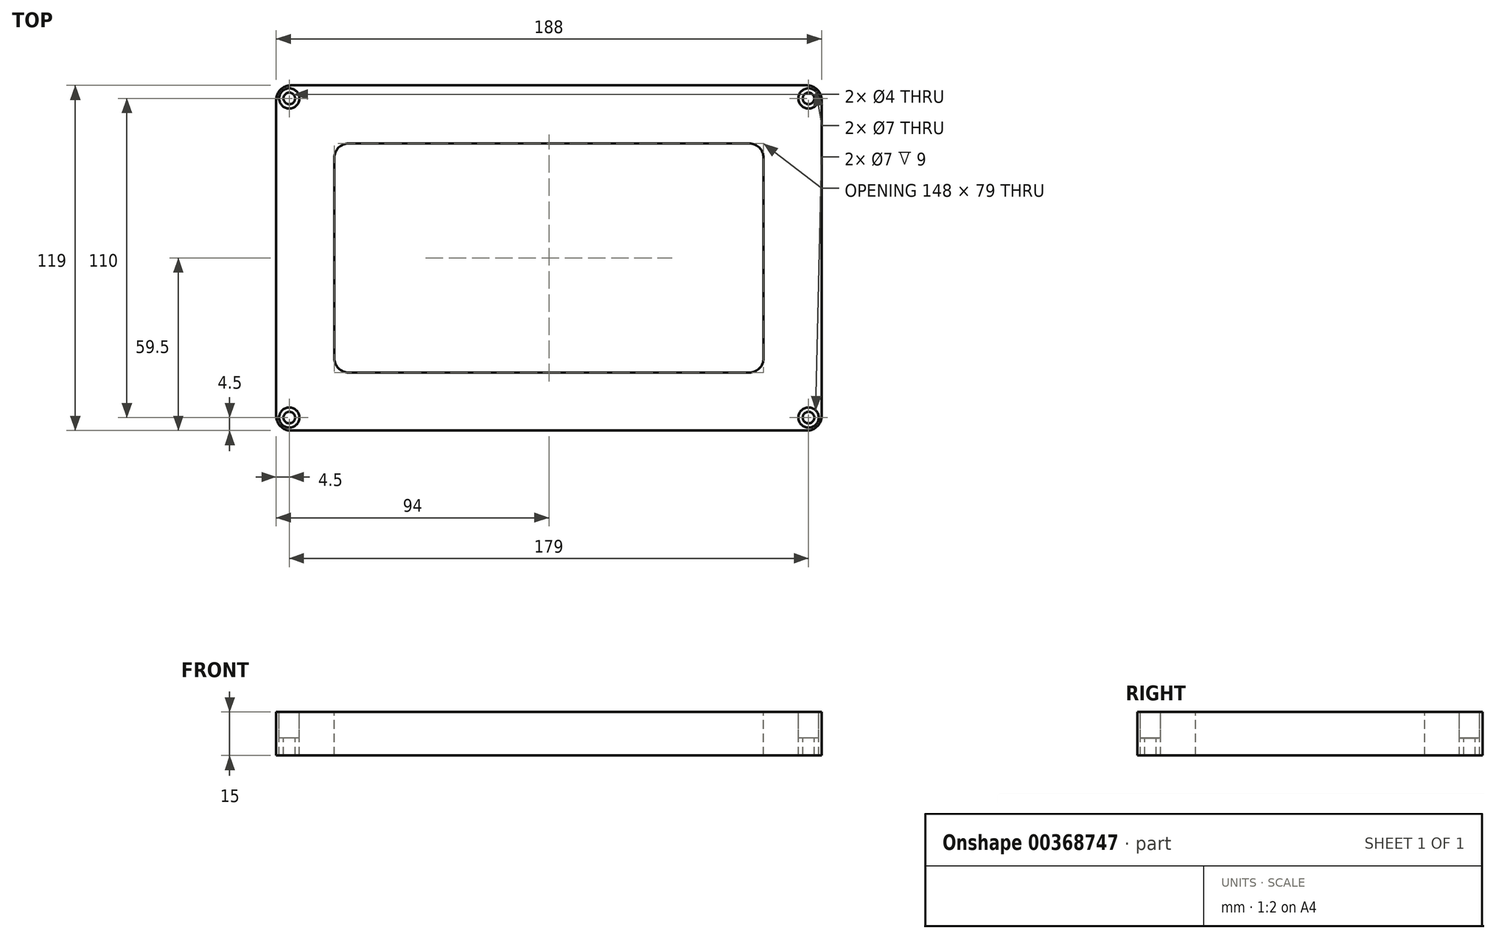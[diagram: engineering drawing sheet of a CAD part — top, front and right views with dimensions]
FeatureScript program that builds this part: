
annotation { "Feature Type Name" : "Feature", "Feature Type Description" : "" }
export const myFeature = defineFeature(function(context is Context, id is Id, definition is map)
    precondition{}
    {
        {
            var Q0;
            Q0=qCreatedBy(makeId("Top.planeOp"),FACE);
            var sketch = newSketch(context, id + "F0", { "sketchPlane" : qUnion([Q0])});
            skLineSegment(sketch, "E0.bottom", {"start": v(-94, 59.5) * mm, "end": v(94, 59.5) * mm});
            skLineSegment(sketch, "E0.top", {"start": v(-94, -59.5) * mm, "end": v(94, -59.5) * mm});
            skLineSegment(sketch, "E0.left", {"start": v(-94, 59.5) * mm, "end": v(-94, -59.5) * mm});
            skLineSegment(sketch, "E0.right", {"start": v(94, 59.5) * mm, "end": v(94, -59.5) * mm});
            skPoint(sketch, "E0.middle", {"position": v(0, 0) * mm});
            skCircle(sketch, "E1", {"center": v(-89.5, 55) * mm, "radius": 2 * mm});
            skCircle(sketch, "E2.MirrorC", {"center": v(89.5, 55) * mm, "radius": 2 * mm});
            skCircle(sketch, "E3.MirrorC", {"center": v(-89.5, -55) * mm, "radius": 2 * mm});
            skCircle(sketch, "E4.MirrorC", {"center": v(89.5, -55) * mm, "radius": 2 * mm});
            skLineSegment(sketch, "E5.bottom", {"start": v(-74, 39.5) * mm, "end": v(74, 39.5) * mm});
            skLineSegment(sketch, "E5.top", {"start": v(-74, -39.5) * mm, "end": v(74, -39.5) * mm});
            skLineSegment(sketch, "E5.left", {"start": v(-74, 39.5) * mm, "end": v(-74, -39.5) * mm});
            skLineSegment(sketch, "E5.right", {"start": v(74, 39.5) * mm, "end": v(74, -39.5) * mm});
            skCircle(sketch, "E6", {"center": v(-89.5, 55) * mm, "radius": 3.5 * mm});
            skCircle(sketch, "E7.MirrorC", {"center": v(89.5, 55) * mm, "radius": 3.5 * mm});
            skCircle(sketch, "E8.MirrorC", {"center": v(-89.5, -55) * mm, "radius": 3.5 * mm});
            skCircle(sketch, "E9.MirrorC", {"center": v(89.5, -55) * mm, "radius": 3.5 * mm});
            skSolve(sketch);
        }
        {
            var Q0;
            Q0=makeQuery(id+"F0.imprint","IMPRINT",FACE,{"disambiguationData":[TD([[makeQuery(id+"F0.imprint","IMPRINT",EDGE,{"derivedFrom":sQuery(id+"F0.wireOp",EDGE,"E0.bottom")}),-1.0]])]});
            var Q1;
            Q1=makeQuery(id+"F0.imprint","IMPRINT",FACE,{"disambiguationData":[TD([[makeQuery(id+"F0.imprint","IMPRINT",EDGE,{"derivedFrom":sQuery(id+"F0.wireOp",EDGE,"E1")}),-1.0]])]});
            var Q2;
            Q2=makeQuery(id+"F0.imprint","IMPRINT",FACE,{"disambiguationData":[TD([[makeQuery(id+"F0.imprint","IMPRINT",EDGE,{"derivedFrom":sQuery(id+"F0.wireOp",EDGE,"E2.MirrorC")}),1.0]])]});
            var Q3;
            Q3=makeQuery(id+"F0.imprint","IMPRINT",FACE,{"disambiguationData":[TD([[makeQuery(id+"F0.imprint","IMPRINT",EDGE,{"derivedFrom":sQuery(id+"F0.wireOp",EDGE,"E4.MirrorC")}),-1.0]])]});
            var Q4;
            Q4=makeQuery(id+"F0.imprint","IMPRINT",FACE,{"disambiguationData":[TD([[makeQuery(id+"F0.imprint","IMPRINT",EDGE,{"derivedFrom":sQuery(id+"F0.wireOp",EDGE,"E3.MirrorC")}),1.0]])]});
            extrude(context, id + "F1", {"entities" : qUnion([Q0, Q1, Q2, Q3, Q4]), "oppositeDirection" : true, "depth" : 15 * mm, "offsetDistance" : 25 * mm});
        }
        {
            var Q0;
            Q0=makeQuery(id+"F0.imprint","IMPRINT",FACE,{"disambiguationData":[TD([[makeQuery(id+"F0.imprint","IMPRINT",EDGE,{"derivedFrom":sQuery(id+"F0.wireOp",EDGE,"E1")}),-1.0]])]});
            var Q1;
            Q1=makeQuery(id+"F0.imprint","IMPRINT",FACE,{"disambiguationData":[TD([[makeQuery(id+"F0.imprint","IMPRINT",EDGE,{"derivedFrom":sQuery(id+"F0.wireOp",EDGE,"E2.MirrorC")}),1.0]])]});
            var Q2;
            Q2=makeQuery(id+"F0.imprint","IMPRINT",FACE,{"disambiguationData":[TD([[makeQuery(id+"F0.imprint","IMPRINT",EDGE,{"derivedFrom":sQuery(id+"F0.wireOp",EDGE,"E4.MirrorC")}),-1.0]])]});
            var Q3;
            Q3=makeQuery(id+"F0.imprint","IMPRINT",FACE,{"disambiguationData":[TD([[makeQuery(id+"F0.imprint","IMPRINT",EDGE,{"derivedFrom":sQuery(id+"F0.wireOp",EDGE,"E3.MirrorC")}),1.0]])]});
            extrude(context, id + "F2", {"entities" : qUnion([Q0, Q1, Q2, Q3]), "operationType" : NewBodyOperationType.REMOVE, "oppositeDirection" : true, "depth" : 9 * mm, "offsetDistance" : 25 * mm});
        }
        {
            var Q0;
            Q0=makeQuery(id+"F1.opExtrude","SWEPT_EDGE",EDGE,{"disambiguationData":[OSD([sQuery(id+"F0.wireOp",EDGE,"E0.bottom"),sQuery(id+"F0.wireOp",EDGE,"E0.right")])]});
            var Q1;
            Q1=makeQuery(id+"F1.opExtrude","SWEPT_EDGE",EDGE,{"disambiguationData":[OSD([sQuery(id+"F0.wireOp",EDGE,"E0.bottom"),sQuery(id+"F0.wireOp",EDGE,"E0.left")])]});
            var Q2;
            Q2=makeQuery(id+"F1.opExtrude","SWEPT_EDGE",EDGE,{"disambiguationData":[OSD([sQuery(id+"F0.wireOp",EDGE,"E0.top"),sQuery(id+"F0.wireOp",EDGE,"E0.left")])]});
            var Q3;
            Q3=makeQuery(id+"F1.opExtrude","SWEPT_EDGE",EDGE,{"disambiguationData":[OSD([sQuery(id+"F0.wireOp",EDGE,"E0.top"),sQuery(id+"F0.wireOp",EDGE,"E0.right")])]});
            var Q4;
            Q4=makeQuery(id+"F1.opExtrude","SWEPT_EDGE",EDGE,{"disambiguationData":[OSD([sQuery(id+"F0.wireOp",EDGE,"E5.bottom"),sQuery(id+"F0.wireOp",EDGE,"E5.left")])]});
            var Q5;
            Q5=makeQuery(id+"F1.opExtrude","SWEPT_EDGE",EDGE,{"disambiguationData":[OSD([sQuery(id+"F0.wireOp",EDGE,"E5.bottom"),sQuery(id+"F0.wireOp",EDGE,"E5.right")])]});
            var Q6;
            Q6=makeQuery(id+"F1.opExtrude","SWEPT_EDGE",EDGE,{"disambiguationData":[OSD([sQuery(id+"F0.wireOp",EDGE,"E5.top"),sQuery(id+"F0.wireOp",EDGE,"E5.right")])]});
            var Q7;
            Q7=makeQuery(id+"F1.opExtrude","SWEPT_EDGE",EDGE,{"disambiguationData":[OSD([sQuery(id+"F0.wireOp",EDGE,"E5.top"),sQuery(id+"F0.wireOp",EDGE,"E5.left")])]});
            fillet(context, id + "F3", {"entities" : qUnion([Q0, Q1, Q2, Q3, Q4, Q5, Q6, Q7]), "radius" : 5 * mm, "tangentPropagation" : true, "allowEdgeOverflow" : false});
        }
    });
